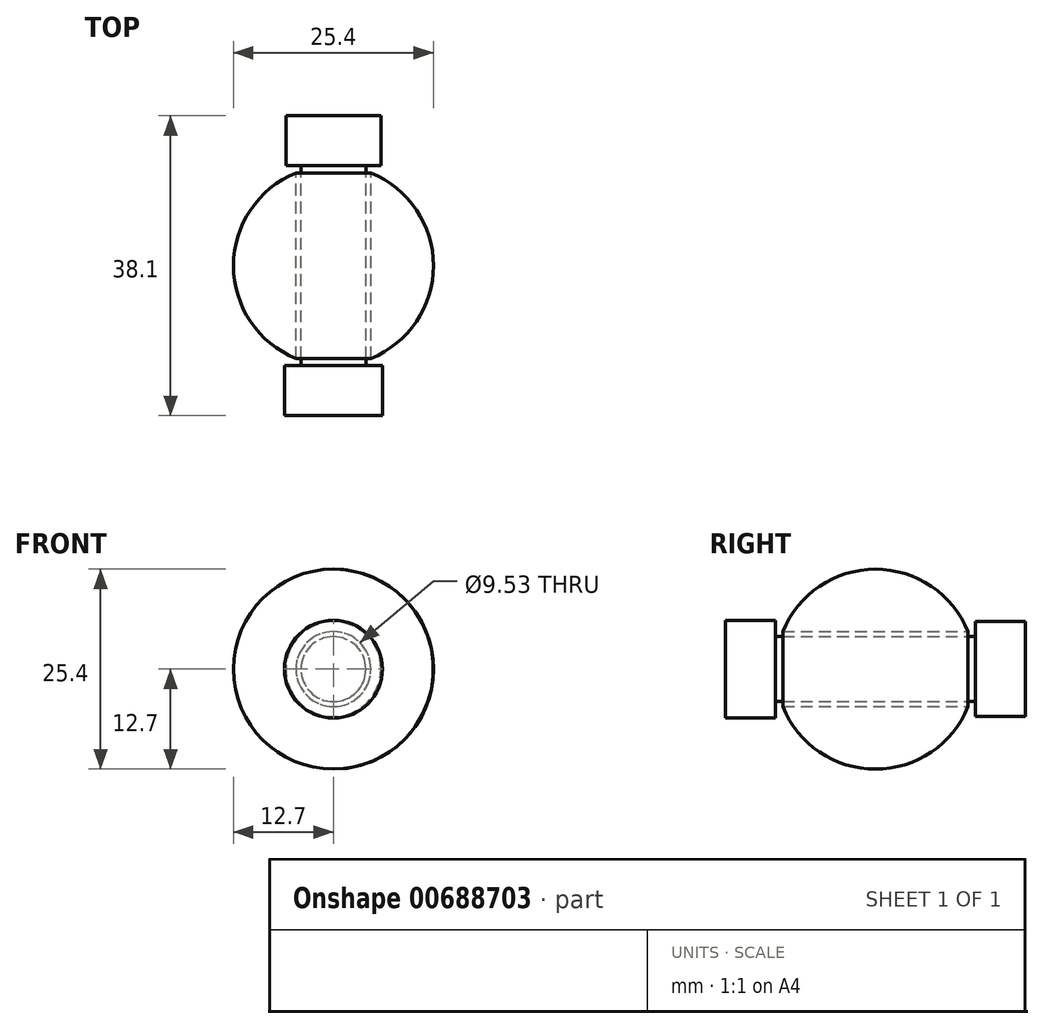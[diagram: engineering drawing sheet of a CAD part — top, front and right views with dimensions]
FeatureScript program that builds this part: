
annotation { "Feature Type Name" : "Feature", "Feature Type Description" : "" }
export const myFeature = defineFeature(function(context is Context, id is Id, definition is map)
    precondition{}
    {
        {
            var Q0;
            Q0=qCreatedBy(makeId("Front.planeOp"),FACE);
            var sketch = newSketch(context, id + "F0", { "sketchPlane" : qUnion([Q0])});
            skArc(sketch, "E0", {"start": v(0, -12.7) * mm, "mid": v(12.7, 0) * mm, "end": v(0, 12.7) * mm});
            skLineSegment(sketch, "E1", {"start": v(0, 12.7) * mm, "end": v(0, -12.7) * mm});
            skSolve(sketch);
        }
        {
            var Q0;
            Q0=makeQuery(id+"F0.imprint","IMPRINT",FACE,{"disambiguationData":[TD([[makeQuery(id+"F0.imprint","IMPRINT",EDGE,{"derivedFrom":sQuery(id+"F0.wireOp",EDGE,"E0")}),1.0]])]});
            var Q1;
            Q1=sQuery(id+"F0.wireOp",EDGE,"E1");
            revolve(context, id + "F1", {"entities" : qUnion([Q0]), "axis" : qUnion([Q1]), "revolveType" : RevolveType.FULL});
        }
        {
            var Q0;
            Q0=qCreatedBy(makeId("Front.planeOp"),FACE);
            var sketch = newSketch(context, id + "F2", { "sketchPlane" : qUnion([Q0])});
            skCircle(sketch, "E2", {"center": v(0, 0) * mm, "radius": 4.76 * mm});
            skSolve(sketch);
        }
        {
            var Q0;
            Q0 = qSketchRegion(id + "F2", true);
            extrude(context, id + "F3", {"entities" : qUnion([Q0]), "operationType" : NewBodyOperationType.REMOVE, "endBound" : BoundingType.SYMMETRIC, "depth" : 127 * mm, "offsetDistance" : 25.4 * mm});
        }
        {
            var Q0;
            Q0=qCreatedBy(makeId("Front.planeOp"),FACE);
            var sketch = newSketch(context, id + "F4", { "sketchPlane" : qUnion([Q0])});
            skCircle(sketch, "E3", {"center": v(0, 0) * mm, "radius": 4.13 * mm});
            skSolve(sketch);
        }
        {
            var Q0;
            Q0=makeQuery(id+"F4.imprint","IMPRINT",FACE,{"disambiguationData":[TD([[makeQuery(id+"F4.imprint","IMPRINT",EDGE,{"derivedFrom":sQuery(id+"F4.wireOp",EDGE,"E3")}),1.0]])]});
            extrude(context, id + "F5", {"entities" : qUnion([Q0]), "endBound" : BoundingType.SYMMETRIC, "depth" : 38.1 * mm, "offsetDistance" : 25.4 * mm});
        }
        {
            var Q0;
            Q0=makeQuery(id+"F5.opExtrude","CAP_FACE",FACE,{"disambiguationData":[OSD([sQuery(id+"F4.wireOp",EDGE,"E3")])],"isStart":false});
            var sketch = newSketch(context, id + "F6", { "sketchPlane" : qUnion([Q0])});
            skCircle(sketch, "E4", {"center": v(0, 0) * mm, "radius": 6.21 * mm});
            skSolve(sketch);
        }
        {
            var Q0;
            Q0=makeQuery(id+"F6.imprint","IMPRINT",FACE,{"disambiguationData":[TD([[makeQuery(id+"F6.imprint","IMPRINT",EDGE,{"derivedFrom":sQuery(id+"F6.wireOp",EDGE,"E4")}),1.0]])]});
            var Q1;
            Q1=sQuery(id+"F6.wireOp",EDGE,"E4");
            extrude(context, id + "F7", {"entities" : qUnion([Q0]), "operationType" : NewBodyOperationType.ADD, "surfaceEntities" : qUnion([Q1]), "oppositeDirection" : true, "depth" : 6.35 * mm, "offsetDistance" : 25.4 * mm});
        }
        {
            var Q0;
            Q0=makeQuery(id+"F5.opExtrude","CAP_FACE",FACE,{"disambiguationData":[OSD([sQuery(id+"F4.wireOp",EDGE,"E3")])],"isStart":true});
            var sketch = newSketch(context, id + "F8", { "sketchPlane" : qUnion([Q0])});
            skCircle(sketch, "E5", {"center": v(0, 0) * mm, "radius": 6.03 * mm});
            skSolve(sketch);
        }
        {
            var Q0;
            Q0 = qSketchRegion(id + "F8", true);
            extrude(context, id + "F9", {"entities" : qUnion([Q0]), "operationType" : NewBodyOperationType.ADD, "oppositeDirection" : true, "depth" : 6.35 * mm, "offsetDistance" : 25.4 * mm});
        }
    });
